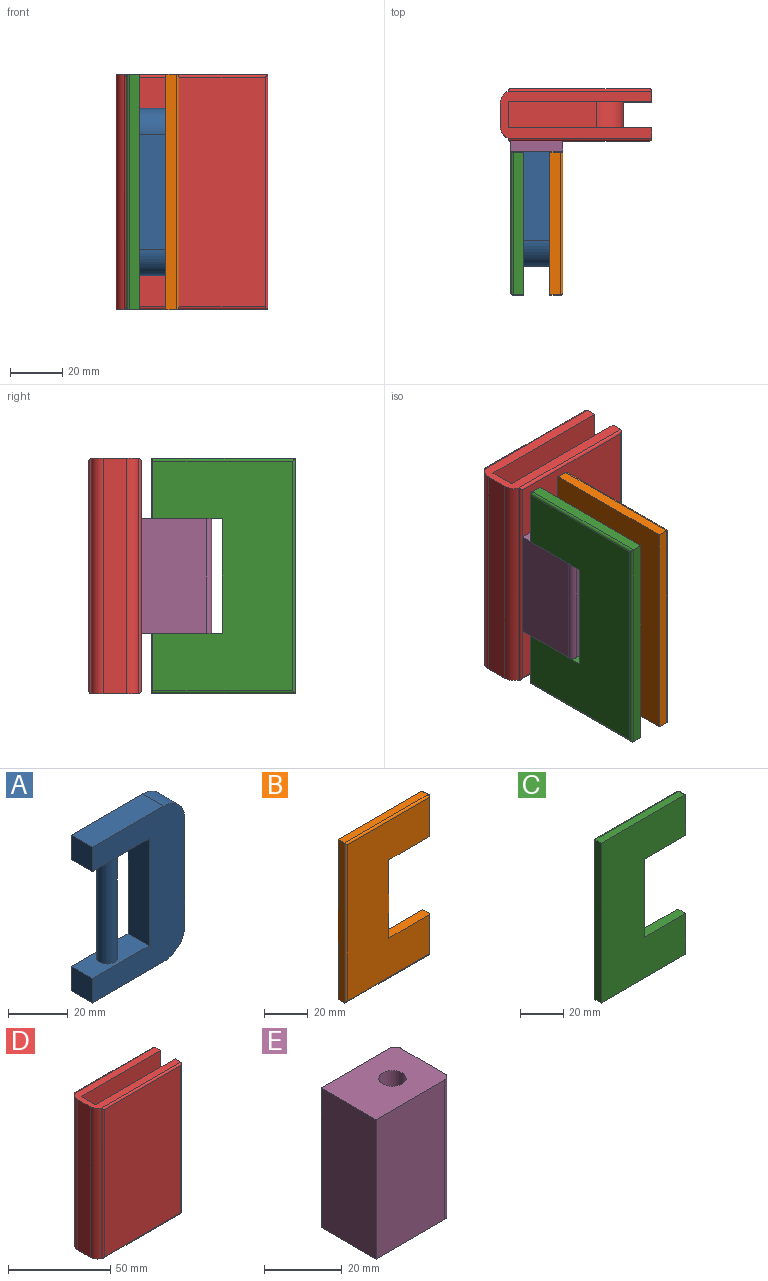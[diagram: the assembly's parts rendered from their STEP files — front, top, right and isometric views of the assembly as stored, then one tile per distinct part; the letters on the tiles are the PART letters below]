
ASSEMBLY  parts=5 mates=4
PART A: 13 faces, bbox 44x10x64 mm
  f0: plane 27x10mm, normal (0,0,-1), area 231.5mm2, adj f1,f9,f10,f11,f12
  f1: plane 44x10mm, normal (-1,0,0), area 440mm2, adj f0,f2,f10,f11
  f2: plane 27x10mm, normal (0,0,1), area 231.5mm2, adj f1,f3,f10,f11,f12
  f3: plane 10x10mm, normal (-1,0,0), area 100mm2, adj f2,f4,f10,f11
  f4: plane 34x10mm, normal (0,0,-1), area 340mm2, adj f3,f5,f10,f11
  f5: cylinder r=10mm len=10mm, axis (0,1,0), area 157.1mm2, adj f4,f6,f10,f11
  f6: plane 44x10mm, normal (1,0,0), area 440mm2, adj f5,f7,f10,f11
  f7: cylinder r=10mm len=10mm, axis (0,1,0), area 157.1mm2, adj f6,f8,f10,f11
  f8: plane 34x10mm, normal (0,0,1), area 340mm2, adj f7,f9,f10,f11
  f9: plane 10x10mm, normal (-1,0,0), area 100mm2, adj f0,f8,f10,f11
  f10: plane 64x44mm, normal (0,-1,0), area 1585.1mm2, adj f0,f1,f2,f3,f4,f5,f6,f7
  f11: plane 64x44mm, normal (0,1,0), area 1585.1mm2, adj f0,f1,f2,f3,f4,f5,f6,f7
  f12: cylinder r=3.5mm len=44mm, axis (0,0,-1), area 967.6mm2, adj f0,f2
PART B: 19 faces, bbox 55x5.1x90.2 mm
  f0: plane 90x4mm, normal (-1,0,0), area 360mm2, adj f1,f7,f9,f11
  f1: plane 54.5x4mm, normal (0,0,-1), area 218mm2, adj f0,f9,f12,f15
  f2: plane 22.5x4.5mm, normal (1,0,0), area 101.2mm2, adj f3,f9,f13,f14,f15
  f3: plane 27x5mm, normal (0,0,1), area 134.9mm2, adj f2,f4,f8,f9,f13
  f4: plane 44x5mm, normal (1,0,0), area 220mm2, adj f3,f5,f8,f9
  f5: plane 27x5mm, normal (0,0,-1), area 134.9mm2, adj f4,f6,f8,f9,f16
  f6: plane 22.5x4.5mm, normal (1,0,0), area 101.2mm2, adj f5,f9,f16,f17,f18
  f7: plane 54.5x4mm, normal (0,0,1), area 218mm2, adj f0,f9,f10,f18
  f8: plane 88x53.5mm, normal (0,-1,0), area 3542mm2, adj f3,f4,f5,f10,f11,f12,f13,f16
  f9: plane 90x55mm, normal (0,1,0), area 3761.9mm2, adj f0,f1,f2,f3,f4,f5,f6,f7
  f10: cylinder r=1mm len=54.5mm, axis (1,0,0), area 85mm2, adj f7,f8,f11,f17
  f11: cylinder r=1mm len=90mm, axis (0,0,1), area 140.2mm2, adj f0,f8,f10,f12
  f12: cylinder r=1mm len=54.5mm, axis (-1,0,0), area 85mm2, adj f1,f8,f11,f14
  f13: cylinder r=0.5mm len=22mm, axis (0,0,-1), area 17.3mm2, adj f2,f3,f8,f14
  f14: torus R=0.5mm, axis (-1,0,0), area 1mm2, adj f2,f12,f13,f15
  f15: cylinder r=0.5mm len=4mm, axis (0,1,0), area 3.1mm2, adj f1,f2,f9,f14
  f16: cylinder r=0.5mm len=22mm, axis (0,0,-1), area 17.3mm2, adj f5,f6,f8,f17
  f17: torus R=0.5mm, axis (-1,0,0), area 1mm2, adj f6,f10,f16,f18
  f18: cylinder r=0.5mm len=4mm, axis (0,-1,0), area 3.1mm2, adj f6,f7,f9,f17
PART C: 19 faces, bbox 55x5.1x90.2 mm
  f0: plane 90x4mm, normal (-1,0,0), area 360mm2, adj f1,f7,f9,f11
  f1: plane 54.5x4mm, normal (0,0,-1), area 218mm2, adj f0,f9,f12,f15
  f2: plane 22.5x4.5mm, normal (1,0,0), area 101.2mm2, adj f3,f9,f13,f14,f15
  f3: plane 27x5mm, normal (0,0,1), area 134.9mm2, adj f2,f4,f8,f9,f13
  f4: plane 44x5mm, normal (1,0,0), area 220mm2, adj f3,f5,f8,f9
  f5: plane 27x5mm, normal (0,0,-1), area 134.9mm2, adj f4,f6,f8,f9,f16
  f6: plane 22.5x4.5mm, normal (1,0,0), area 101.2mm2, adj f5,f9,f16,f17,f18
  f7: plane 54.5x4mm, normal (0,0,1), area 218mm2, adj f0,f9,f10,f18
  f8: plane 88x53.5mm, normal (0,1,0), area 3542mm2, adj f3,f4,f5,f10,f11,f12,f13,f16
  f9: plane 90x55mm, normal (0,-1,0), area 3761.9mm2, adj f0,f1,f2,f3,f4,f5,f6,f7
  f10: cylinder r=1mm len=54.5mm, axis (1,0,0), area 85mm2, adj f7,f8,f11,f17
  f11: cylinder r=1mm len=90mm, axis (0,0,1), area 140.2mm2, adj f0,f8,f10,f12
  f12: cylinder r=1mm len=54.5mm, axis (-1,0,0), area 85mm2, adj f1,f8,f11,f14
  f13: cylinder r=0.5mm len=22mm, axis (0,0,-1), area 17.3mm2, adj f2,f3,f8,f14
  f14: torus R=0.5mm, axis (-1,0,0), area 1mm2, adj f2,f12,f13,f15
  f15: cylinder r=0.5mm len=4mm, axis (0,-1,0), area 3.1mm2, adj f1,f2,f9,f14
  f16: cylinder r=0.5mm len=22mm, axis (0,0,-1), area 17.3mm2, adj f5,f6,f8,f17
  f17: torus R=0.5mm, axis (-1,0,0), area 1mm2, adj f6,f10,f16,f18
  f18: cylinder r=0.5mm len=4mm, axis (0,1,0), area 3.1mm2, adj f6,f7,f9,f17
PART D: 26 faces, bbox 58x20x90 mm
  f0: plane 90x55mm, normal (0,1,0), area 2176.9mm2, adj f1,f2,f3,f16,f17,f18,f19,f20
  f1: plane 58x18mm, normal (0,0,-1), area 486.3mm2, adj f0,f2,f6,f9,f11,f13,f22,f23
  f2: plane 90x4mm, normal (1,0,0), area 360mm2, adj f0,f1,f3,f8
  f3: plane 58x18mm, normal (0,0,1), area 486.3mm2, adj f0,f2,f7,f9,f11,f14,f21,f23
  f4: plane 88x53mm, normal (0,-1,0), area 4664mm2, adj f5,f6,f7,f8
  f5: cylinder r=1mm len=90mm, axis (0,0,1), area 140.2mm2, adj f4,f6,f7,f24
  f6: cylinder r=1mm len=55mm, axis (-1,0,0), area 85.3mm2, adj f1,f4,f5,f8
  f7: cylinder r=1mm len=55mm, axis (1,0,0), area 85.3mm2, adj f3,f4,f5,f8
  f8: cylinder r=1mm len=90mm, axis (0,0,-1), area 140.2mm2, adj f2,f4,f6,f7
  f9: plane 90x4mm, normal (1,0,0), area 360mm2, adj f1,f3,f11,f15
  f10: plane 88x53mm, normal (0,1,0), area 4664mm2, adj f12,f13,f14,f15
  f11: plane 90x55mm, normal (0,-1,0), area 2176.9mm2, adj f1,f3,f9,f16,f17,f18,f19,f20
  f12: cylinder r=1mm len=90mm, axis (0,0,1), area 140.2mm2, adj f10,f13,f14,f25
  f13: cylinder r=1mm len=55mm, axis (-1,0,0), area 85.3mm2, adj f1,f10,f12,f15
  f14: cylinder r=1mm len=55mm, axis (1,0,0), area 85.3mm2, adj f3,f10,f12,f15
  f15: cylinder r=1mm len=90mm, axis (0,0,-1), area 140.2mm2, adj f9,f10,f13,f14
  f16: plane 34x10mm, normal (0,0,1), area 340mm2, adj f0,f11,f20,f21
  f17: plane 34x10mm, normal (0,0,-1), area 340mm2, adj f0,f11,f18,f22
  f18: cylinder r=10mm len=10mm, axis (0,1,0), area 157.1mm2, adj f0,f11,f17,f19
  f19: plane 44x10mm, normal (1,0,0), area 440mm2, adj f0,f11,f18,f20
  f20: cylinder r=10mm len=10mm, axis (0,1,0), area 157.1mm2, adj f0,f11,f16,f19
  f21: plane 13x10mm, normal (1,0,0), area 130mm2, adj f0,f3,f11,f16
  f22: plane 13x10mm, normal (1,0,0), area 130mm2, adj f0,f1,f11,f17
  f23: plane 90x8.84mm, normal (-1,0,0), area 795.1mm2, adj f1,f3,f24,f25
  f24: cylinder r=5mm len=90mm, axis (0,0,1), area 521.7mm2, adj f1,f3,f5,f23
  f25: cylinder r=5mm len=90mm, axis (0,0,1), area 521.7mm2, adj f1,f3,f12,f23
PART E: 9 faces, bbox 27x20x44 mm
  f0: plane 44x25mm, normal (0,1,0), area 1100mm2, adj f1,f5,f7,f8
  f1: plane 44x20mm, normal (-1,0,0), area 880mm2, adj f0,f2,f7,f8
  f2: plane 44x25mm, normal (0,-1,0), area 1100mm2, adj f1,f3,f7,f8
  f3: cylinder r=2mm len=44mm, axis (0,0,-1), area 138.2mm2, adj f2,f4,f7,f8
  f4: plane 44x16mm, normal (1,0,0), area 704mm2, adj f3,f5,f7,f8
  f5: cylinder r=2mm len=44mm, axis (0,0,-1), area 138.2mm2, adj f0,f4,f7,f8
  f6: cylinder r=3.5mm len=44mm, axis (0,0,-1), area 967.6mm2, adj f7,f8
  f7: plane 27x20mm, normal (0,0,1), area 499.8mm2, adj f0,f1,f2,f3,f4,f5,f6
  f8: plane 27x20mm, normal (0,0,-1), area 499.8mm2, adj f0,f1,f2,f3,f4,f5,f6
PLACE A rot(axis=(0,0,-1),90deg) t=(-16.65,6.76,-0.72)mm
PLACE B rot(axis=(0,0,1),90deg) t=(-16.65,-48.24,-13.72)mm
PLACE C rot(axis=(0,0,1),90deg) t=(-16.65,-48.24,-13.72)mm
PLACE D t=(-27.65,20.76,-13.72)mm fixed
PLACE E rot(axis=(0,0,-1),90deg) t=(-16.65,10.76,9.28)mm
MATE fastened D.f4 <-> E.f1  axis (0,-1,0) through (-26.65,10.76,31.28)mm
MATE revolute E.f6 <-> A.f12  axis (0,0,1) through (-16.65,-5.24,53.28)mm
MATE fastened B.f6 <-> A.f9  axis (0,-1,0) through (-11.65,6.76,53.28)mm
MATE fastened C.f6 <-> A.f9  axis (0,-1,0) through (-21.65,6.76,53.28)mm
